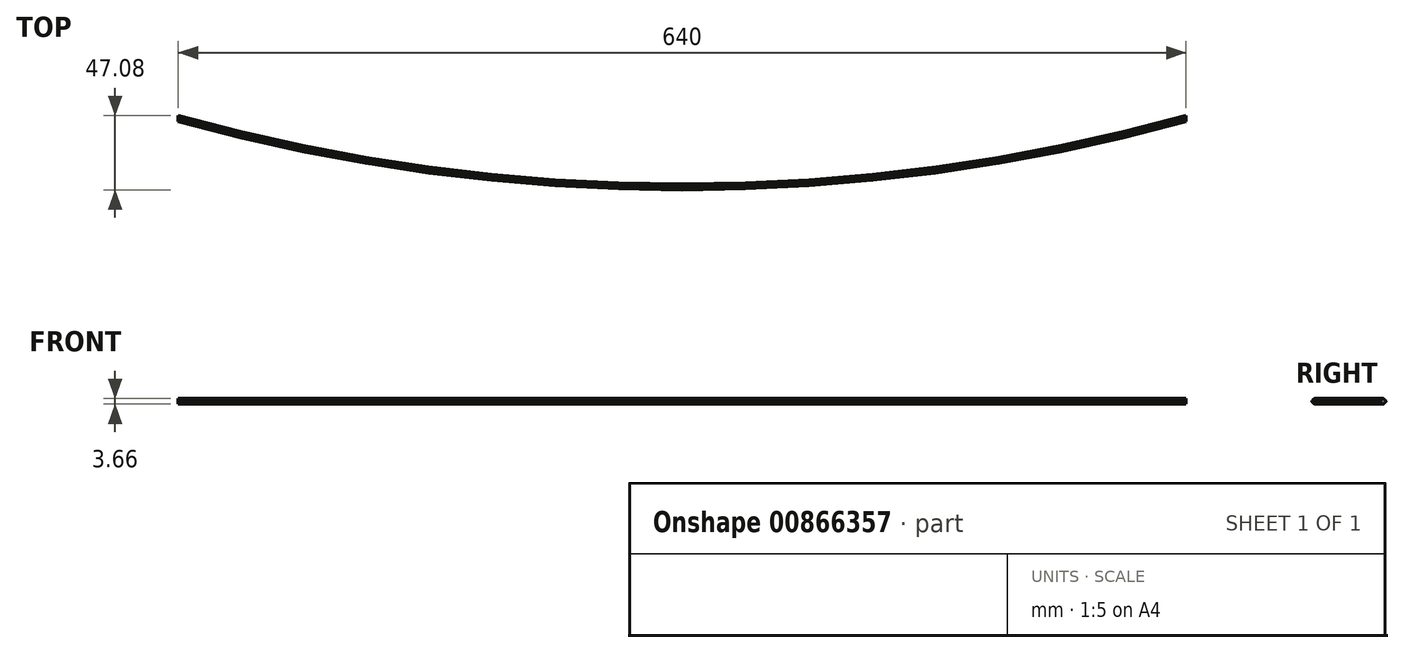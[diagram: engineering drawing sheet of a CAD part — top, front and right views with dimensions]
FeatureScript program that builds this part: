
annotation { "Feature Type Name" : "Feature", "Feature Type Description" : "" }
export const myFeature = defineFeature(function(context is Context, id is Id, definition is map)
    precondition{}
    {
        {
            var Q0;
            Q0=qCreatedBy(makeId("Top.planeOp"),FACE);
            var sketch = newSketch(context, id + "F0", { "sketchPlane" : qUnion([Q0])});
            skArc(sketch, "E0", {"start": v(-299.03, 0) * mm, "mid": v(20.97, -43.45) * mm, "end": v(340.97, 0) * mm});
            skArc(sketch, "E1.0", {"start": v(-299.03, -5.19) * mm, "mid": v(20.97, -48.45) * mm, "end": v(340.97, -5.19) * mm});
            skLineSegment(sketch, "E2", {"start": v(-299.03, 0) * mm, "end": v(-299.03, -5.19) * mm});
            skPoint(sketch, "E3.orphan", {"position": v(-299.03, -9.75) * mm});
            skLineSegment(sketch, "E4", {"start": v(340.97, 0) * mm, "end": v(340.97, -5.19) * mm});
            skSolve(sketch);
        }
        {
            var Q0;
            Q0=makeQuery(id+"F0.imprint","IMPRINT",FACE,{"disambiguationData":[TD([[makeQuery(id+"F0.imprint","IMPRINT",EDGE,{"derivedFrom":sQuery(id+"F0.wireOp",EDGE,"E0")}),-1.0]])]});
            extrude(context, id + "F1", {"entities" : qUnion([Q0]), "depth" : 5 * mm, "offsetDistance" : 25 * mm});
        }
        {
            var Q0;
            Q0=makeQuery(id+"F1.opExtrude","CAP_EDGE",EDGE,{"disambiguationData":[OSD([sQuery(id+"F0.wireOp",EDGE,"E1.0")])],"isStart":true});
            var Q1;
            Q1=makeQuery(id+"F1.opExtrude","CAP_EDGE",EDGE,{"disambiguationData":[OSD([sQuery(id+"F0.wireOp",EDGE,"E0")])],"isStart":false});
            var Q2;
            Q2=makeQuery(id+"F1.opExtrude","CAP_EDGE",EDGE,{"disambiguationData":[OSD([sQuery(id+"F0.wireOp",EDGE,"E1.0")])],"isStart":false});
            var Q3;
            Q3=makeQuery(id+"F1.opExtrude","CAP_EDGE",EDGE,{"disambiguationData":[OSD([sQuery(id+"F0.wireOp",EDGE,"E0")])],"isStart":true});
            fillet(context, id + "F2", {"entities" : qUnion([Q0, Q1, Q2, Q3]), "radius" : 5 * mm, "tangentPropagation" : true, "allowEdgeOverflow" : false});
        }
    });
